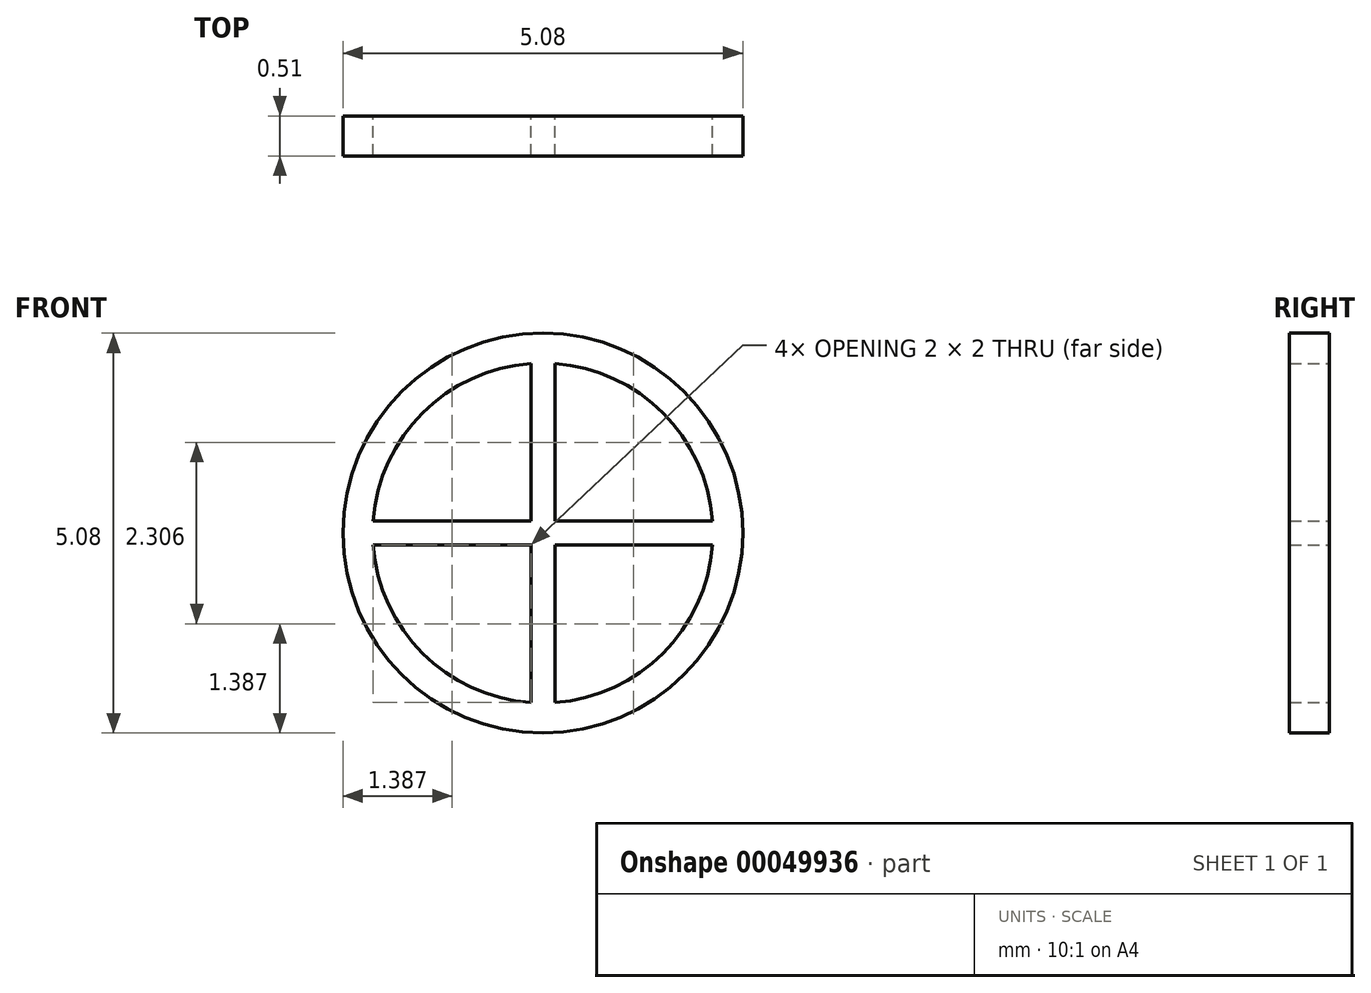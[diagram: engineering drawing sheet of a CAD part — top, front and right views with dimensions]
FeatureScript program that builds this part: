
annotation { "Feature Type Name" : "Feature", "Feature Type Description" : "" }
export const myFeature = defineFeature(function(context is Context, id is Id, definition is map)
    precondition{}
    {
        {
            var Q0;
            Q0=qCreatedBy(makeId("Front.planeOp"),FACE);
            var sketch = newSketch(context, id + "F0", { "sketchPlane" : qUnion([Q0])});
            skLineSegment(sketch, "E0", {"start": v(0, 0) * mm, "end": v(5.08, 0) * mm, "construction": true});
            skLineSegment(sketch, "E1", {"start": v(5.08, 0) * mm, "end": v(5.08, 5.08) * mm, "construction": true});
            skLineSegment(sketch, "E2", {"start": v(5.08, 5.08) * mm, "end": v(0, 5.08) * mm, "construction": true});
            skLineSegment(sketch, "E3", {"start": v(0, 5.08) * mm, "end": v(0, 0) * mm, "construction": true});
            skLineSegment(sketch, "E4", {"start": v(0, 2.54) * mm, "end": v(5.08, 2.54) * mm, "construction": true});
            skLineSegment(sketch, "E5", {"start": v(2.54, 5.08) * mm, "end": v(2.54, 0) * mm, "construction": true});
            skCircle(sketch, "E6", {"center": v(2.54, 2.54) * mm, "radius": 2.54 * mm});
            skLineSegment(sketch, "E7", {"start": v(2.54, 2.54) * mm, "end": v(4.7, 2.54) * mm});
            skCircle(sketch, "E8", {"center": v(2.54, 2.54) * mm, "radius": 2.16 * mm});
            skLineSegment(sketch, "E9", {"start": v(2.54, 2.54) * mm, "end": v(2.54, 2.62) * mm});
            skLineSegment(sketch, "E10", {"start": v(2.54, 2.62) * mm, "end": v(2.7, 2.62) * mm});
            skLineSegment(sketch, "E11", {"start": v(2.7, 2.62) * mm, "end": v(2.7, 2.54) * mm});
            skLineSegment(sketch, "E12", {"start": v(2.54, 2.62) * mm, "end": v(2.39, 2.62) * mm});
            skLineSegment(sketch, "E13", {"start": v(2.39, 2.62) * mm, "end": v(2.39, 2.54) * mm});
            skLineSegment(sketch, "E14", {"start": v(2.39, 2.54) * mm, "end": v(2.54, 2.54) * mm});
            skLineSegment(sketch, "E15", {"start": v(2.39, 2.54) * mm, "end": v(2.39, 2.46) * mm});
            skLineSegment(sketch, "E16", {"start": v(2.7, 2.54) * mm, "end": v(2.7, 2.46) * mm});
            skLineSegment(sketch, "E17", {"start": v(2.39, 2.46) * mm, "end": v(2.7, 2.46) * mm});
            skLineSegment(sketch, "E18", {"start": v(2.39, 2.54) * mm, "end": v(2.39, 2.39) * mm});
            skLineSegment(sketch, "E19", {"start": v(2.39, 2.39) * mm, "end": v(2.31, 2.39) * mm});
            skLineSegment(sketch, "E20", {"start": v(2.39, 2.54) * mm, "end": v(2.39, 2.7) * mm});
            skLineSegment(sketch, "E21", {"start": v(2.39, 2.7) * mm, "end": v(2.31, 2.7) * mm});
            skLineSegment(sketch, "E22", {"start": v(2.31, 2.7) * mm, "end": v(2.31, 2.39) * mm});
            skLineSegment(sketch, "E23", {"start": v(2.39, 2.7) * mm, "end": v(2.7, 2.7) * mm});
            skLineSegment(sketch, "E24", {"start": v(2.39, 2.39) * mm, "end": v(2.7, 2.39) * mm});
            skLineSegment(sketch, "E25", {"start": v(2.7, 2.7) * mm, "end": v(2.77, 2.7) * mm});
            skLineSegment(sketch, "E26", {"start": v(2.7, 2.39) * mm, "end": v(2.77, 2.39) * mm});
            skLineSegment(sketch, "E27", {"start": v(2.77, 2.7) * mm, "end": v(2.77, 2.39) * mm});
            skLineSegment(sketch, "E28", {"start": v(2.54, 2.62) * mm, "end": v(2.54, 2.7) * mm});
            skLineSegment(sketch, "E29", {"start": v(2.77, 2.39) * mm, "end": v(4.7, 2.39) * mm});
            skLineSegment(sketch, "E30", {"start": v(2.77, 2.7) * mm, "end": v(4.7, 2.7) * mm});
            skLineSegment(sketch, "E31", {"start": v(2.7, 2.62) * mm, "end": v(2.7, 4.7) * mm});
            skLineSegment(sketch, "E32", {"start": v(2.39, 2.62) * mm, "end": v(2.39, 4.7) * mm});
            skLineSegment(sketch, "E33", {"start": v(2.31, 2.7) * mm, "end": v(0.39, 2.7) * mm});
            skLineSegment(sketch, "E34", {"start": v(2.31, 2.39) * mm, "end": v(0.39, 2.39) * mm});
            skLineSegment(sketch, "E35", {"start": v(2.39, 2.46) * mm, "end": v(2.39, 0.39) * mm});
            skLineSegment(sketch, "E36", {"start": v(2.7, 2.46) * mm, "end": v(2.7, 0.39) * mm});
            skSolve(sketch);
        }
        {
            var Q0;
            Q0 = qSketchRegion(id + "F0", true);
            var Q1;
            Q1=makeQuery(id+"F0.imprint","IMPRINT",FACE,{"disambiguationData":[TD([[makeQuery(id+"F0.imprint","IMPRINT",EDGE,{"derivedFrom":sQuery(id+"F0.wireOp",EDGE,"E18")}),-1.0]])]});
            var Q2;
            Q2=makeQuery(id+"F0.imprint","IMPRINT",FACE,{"disambiguationData":[TD([[makeQuery(id+"F0.imprint","IMPRINT",EDGE,{"derivedFrom":sQuery(id+"F0.wireOp",EDGE,"E22")}),-1.0]])]});
            var Q3;
            {var subQ5=sQuery(id+"F0.wireOp",EDGE,"E29");Q3=makeQuery(id+"F0.imprint","IMPRINT",FACE,{"disambiguationData":[TD([[makeQuery(id+"F0.imprint","IMPRINT",EDGE,{"derivedFrom":subQ5}),1.0]])]});}
            var Q4;
            {var subQ5=sQuery(id+"F0.wireOp",EDGE,"E26");Q4=makeQuery(id+"F0.imprint","IMPRINT",FACE,{"disambiguationData":[TD([[makeQuery(id+"F0.imprint","IMPRINT",EDGE,{"derivedFrom":subQ5}),1.0]])]});}
            var Q5;
            {var subQ5=sQuery(id+"F0.wireOp",EDGE,"E25");Q5=makeQuery(id+"F0.imprint","IMPRINT",FACE,{"disambiguationData":[TD([[makeQuery(id+"F0.imprint","IMPRINT",EDGE,{"derivedFrom":subQ5}),-1.0]])]});}
            var Q6;
            {var subQ5=sQuery(id+"F0.wireOp",EDGE,"E30");Q6=makeQuery(id+"F0.imprint","IMPRINT",FACE,{"disambiguationData":[TD([[makeQuery(id+"F0.imprint","IMPRINT",EDGE,{"derivedFrom":subQ5}),-1.0]])]});}
            var Q7;
            {var subQ3=sQuery(id+"F0.wireOp",EDGE,"E23");var subQ5=makeQuery(id+"F0.imprint","INTERSECT",VERTEX,{"derivedFrom":[subQ3,sQuery(id+"F0.wireOp",EDGE,"E28")]});Q7=makeQuery(id+"F0.imprint","IMPRINT",FACE,{"disambiguationData":[TD([[makeQuery(id+"F0.imprint","IMPRINT",EDGE,{"disambiguationData":[TD([[subQ5,1.0]])],"derivedFrom":subQ3}),-1.0]])]});}
            var Q8;
            {var subQ0=sQuery(id+"F0.wireOp",EDGE,"E14");Q8=makeQuery(id+"F0.imprint","IMPRINT",FACE,{"disambiguationData":[TD([[makeQuery(id+"F0.imprint","IMPRINT",EDGE,{"derivedFrom":subQ0}),1.0]])]});}
            var Q9;
            {var subQ0=sQuery(id+"F0.wireOp",EDGE,"E14");Q9=makeQuery(id+"F0.imprint","IMPRINT",FACE,{"disambiguationData":[TD([[makeQuery(id+"F0.imprint","IMPRINT",EDGE,{"derivedFrom":subQ0}),-1.0]])]});}
            var Q10;
            {var subQ3=sQuery(id+"F0.wireOp",EDGE,"E28");Q10=makeQuery(id+"F0.imprint","IMPRINT",FACE,{"disambiguationData":[TD([[makeQuery(id+"F0.imprint","IMPRINT",EDGE,{"derivedFrom":subQ3}),-1.0]])]});}
            var Q11;
            {var subQ0=sQuery(id+"F0.wireOp",EDGE,"E12");Q11=makeQuery(id+"F0.imprint","IMPRINT",FACE,{"disambiguationData":[TD([[makeQuery(id+"F0.imprint","IMPRINT",EDGE,{"derivedFrom":subQ0}),1.0]])]});}
            var Q12;
            {var subQ5=sQuery(id+"F0.wireOp",EDGE,"E28");Q12=makeQuery(id+"F0.imprint","IMPRINT",FACE,{"disambiguationData":[TD([[makeQuery(id+"F0.imprint","IMPRINT",EDGE,{"derivedFrom":subQ5}),1.0]])]});}
            var Q13;
            {var subQ4=sQuery(id+"F0.wireOp",EDGE,"E12");Q13=makeQuery(id+"F0.imprint","IMPRINT",FACE,{"disambiguationData":[TD([[makeQuery(id+"F0.imprint","IMPRINT",EDGE,{"derivedFrom":subQ4}),-1.0]])]});}
            var Q14;
            Q14=makeQuery(id+"F0.imprint","IMPRINT",FACE,{"disambiguationData":[TD([[makeQuery(id+"F0.imprint","IMPRINT",EDGE,{"derivedFrom":sQuery(id+"F0.wireOp",EDGE,"E15")}),1.0]])]});
            var Q15;
            Q15=makeQuery(id+"F0.imprint","IMPRINT",FACE,{"disambiguationData":[TD([[makeQuery(id+"F0.imprint","IMPRINT",EDGE,{"derivedFrom":sQuery(id+"F0.wireOp",EDGE,"E17")}),-1.0]])]});
            var Q16;
            {var subQ3=sQuery(id+"F0.wireOp",EDGE,"E9");Q16=makeQuery(id+"F0.imprint","IMPRINT",FACE,{"disambiguationData":[TD([[makeQuery(id+"F0.imprint","IMPRINT",EDGE,{"derivedFrom":subQ3}),-1.0]])]});}
            var Q17;
            {var subQ0=sQuery(id+"F0.wireOp",EDGE,"E31");var subQ6=sQuery(id+"F0.wireOp",EDGE,"E8");var subQ7=makeQuery(id+"F0.imprint","INTERSECT",VERTEX,{"derivedFrom":[subQ6,subQ0]});Q17=makeQuery(id+"F0.imprint","IMPRINT",FACE,{"disambiguationData":[TD([[makeQuery(id+"F0.imprint","IMPRINT",EDGE,{"disambiguationData":[TD([[subQ7,-1.0]])],"derivedFrom":subQ6}),1.0]])]});}
            var Q18;
            {var subQ5=sQuery(id+"F0.wireOp",EDGE,"E24");Q18=makeQuery(id+"F0.imprint","IMPRINT",FACE,{"disambiguationData":[TD([[makeQuery(id+"F0.imprint","IMPRINT",EDGE,{"derivedFrom":subQ5}),-1.0]])]});}
            extrude(context, id + "F1", {"entities" : qUnion([Q0, Q1, Q2, Q3, Q4, Q5, Q6, Q7, Q8, Q9, Q10, Q11, Q12, Q13, Q14, Q15, Q16, Q17, Q18]), "depth" : 0.5 * mm});
        }
    });
